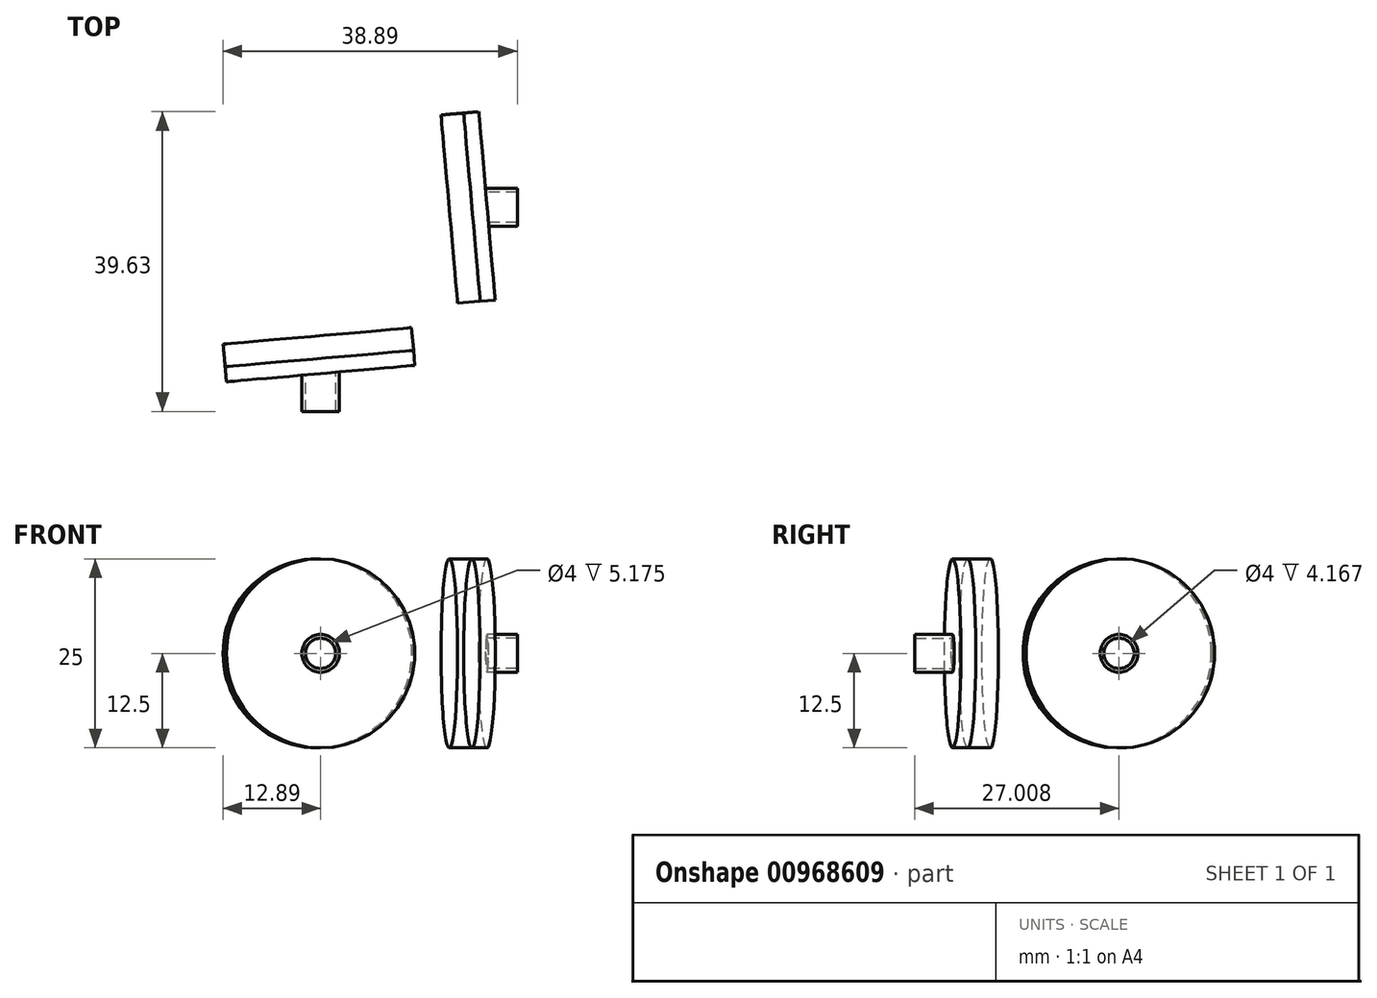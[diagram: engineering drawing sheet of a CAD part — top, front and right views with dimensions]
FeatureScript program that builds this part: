
annotation { "Feature Type Name" : "Feature", "Feature Type Description" : "" }
export const myFeature = defineFeature(function(context is Context, id is Id, definition is map)
    precondition{}
    {
        {
            var Q0;
            Q0=qCreatedBy(makeId("Top.planeOp"),FACE);
            var sketch = newSketch(context, id + "F0", { "sketchPlane" : qUnion([Q0])});
            skLineSegment(sketch, "E0", {"start": v(-12.45, -1.09) * mm, "end": v(0, 0) * mm});
            skLineSegment(sketch, "E1.0", {"start": v(-12.63, 0.9) * mm, "end": v(-0.17, 2) * mm});
            skLineSegment(sketch, "E2", {"start": v(-12.63, 0.9) * mm, "end": v(-12.45, -1.09) * mm});
            skLineSegment(sketch, "E3", {"start": v(-0.17, 2) * mm, "end": v(0, 0) * mm});
            skLineSegment(sketch, "E4", {"start": v(-3.25, 2.3) * mm, "end": v(0.17, 2) * mm, "construction": true});
            skLineSegment(sketch, "E5", {"start": v(-20, 22) * mm, "end": v(0, 2) * mm, "construction": true});
            skLineSegment(sketch, "E6", {"start": v(0.92, 12.5) * mm, "end": v(0, 2) * mm, "construction": true});
            skLineSegment(sketch, "E7", {"start": v(-0.82, 11.4) * mm, "end": v(0, 2) * mm, "construction": true});
            skLineSegment(sketch, "E8.MirrorCS", {"start": v(16.22, 25.18) * mm, "end": v(0, 2) * mm, "construction": true});
            skLineSegment(sketch, "E9.MirrorCS", {"start": v(23.17, 18.23) * mm, "end": v(0, 2) * mm, "construction": true});
            skLineSegment(sketch, "E10.MirrorCS", {"start": v(20, 22) * mm, "end": v(0, 2) * mm, "construction": true});
            skLineSegment(sketch, "E11", {"start": v(-20, 9.08) * mm, "end": v(-20, -14.55) * mm, "construction": true});
            skLineSegment(sketch, "E12", {"start": v(20, 39) * mm, "end": v(20, -14.55) * mm, "construction": true});
            skLineSegment(sketch, "E13", {"start": v(-20, -14.55) * mm, "end": v(0, -14.55) * mm, "construction": true});
            skLineSegment(sketch, "E14", {"start": v(20, -14.55) * mm, "end": v(0, -14.55) * mm, "construction": true});
            skLineSegment(sketch, "E15", {"start": v(18.91, 34.46) * mm, "end": v(20, 22) * mm});
            skLineSegment(sketch, "E16.0", {"start": v(20.9, 34.63) * mm, "end": v(22, 22.18) * mm});
            skLineSegment(sketch, "E17", {"start": v(22, 22.18) * mm, "end": v(20, 22) * mm});
            skLineSegment(sketch, "E18", {"start": v(20.9, 34.63) * mm, "end": v(18.91, 34.46) * mm});
            skSolve(sketch);
        }
        {
            var Q0;
            Q0=makeQuery(id+"F0.imprint","IMPRINT",FACE,{"disambiguationData":[TD([[makeQuery(id+"F0.imprint","IMPRINT",EDGE,{"derivedFrom":sQuery(id+"F0.wireOp",EDGE,"E0")}),1.0]])]});
            var Q1;
            Q1=sQuery(id+"F0.wireOp",EDGE,"E3");
            revolve(context, id + "F1", {"surfaceOperationType" : NewSurfaceOperationType.NEW, "entities" : qUnion([Q0]), "axis" : qUnion([Q1]), "revolveType" : RevolveType.FULL});
        }
        {
            var Q0;
            Q0=qCreatedBy(makeId("Front.planeOp"),FACE);
            var sketch = newSketch(context, id + "F2", { "sketchPlane" : qUnion([Q0])});
            skCircle(sketch, "E19", {"center": v(0, 0) * mm, "radius": 2.5 * mm});
            skCircle(sketch, "E20", {"center": v(0, 0) * mm, "radius": 2 * mm});
            skSolve(sketch);
        }
        {
            var Q0;
            Q0=makeQuery(id+"F2.imprint","IMPRINT",FACE,{"disambiguationData":[TD([[makeQuery(id+"F2.imprint","IMPRINT",EDGE,{"derivedFrom":sQuery(id+"F2.wireOp",EDGE,"E19")}),1.0]])]});
            extrude(context, id + "F3", {"entities" : qUnion([Q0]), "operationType" : NewBodyOperationType.ADD, "depth" : 5 * mm, "offsetDistance" : 25 * mm, "hasSecondDirection" : true, "secondDirectionOppositeDirection" : true, "secondDirectionDepth" : 1 * mm});
        }
        {
            var Q0;
            Q0=makeQuery(id+"F0.imprint","IMPRINT",FACE,{"disambiguationData":[TD([[makeQuery(id+"F0.imprint","IMPRINT",EDGE,{"derivedFrom":sQuery(id+"F0.wireOp",EDGE,"E15")}),1.0]])]});
            var Q1;
            Q1=sQuery(id+"F0.wireOp",EDGE,"E17");
            revolve(context, id + "F4", {"surfaceOperationType" : NewSurfaceOperationType.NEW, "entities" : qUnion([Q0]), "axis" : qUnion([Q1]), "revolveType" : RevolveType.FULL});
        }
        {
            var Q0;
            Q0=qCreatedBy(makeId("Right.planeOp"),FACE);
            var sketch = newSketch(context, id + "F5", { "sketchPlane" : qUnion([Q0])});
            skCircle(sketch, "E21", {"center": v(22, 0) * mm, "radius": 2.5 * mm});
            skCircle(sketch, "E22", {"center": v(22, 0) * mm, "radius": 2 * mm});
            skSolve(sketch);
        }
        {
            var Q0;
            Q0=makeQuery(id+"F5.imprint","IMPRINT",FACE,{"disambiguationData":[TD([[makeQuery(id+"F5.imprint","IMPRINT",EDGE,{"derivedFrom":sQuery(id+"F5.wireOp",EDGE,"E21")}),1.0]])]});
            extrude(context, id + "F6", {"entities" : qUnion([Q0]), "operationType" : NewBodyOperationType.ADD, "depth" : 26 * mm, "offsetDistance" : 25 * mm, "hasSecondDirection" : true, "secondDirectionOppositeDirection" : false, "secondDirectionDepth" : 21 * mm});
        }
        {
            var Q0;
            Q0=makeQuery(id+"F4.opRevolve","SWEPT_FACE",FACE,{"disambiguationData":[OSD([sQuery(id+"F0.wireOp",EDGE,"E15")])]});
            extrude(context, id + "F7", {"entities" : qUnion([Q0]), "depth" : 3 * mm, "offsetDistance" : 25 * mm});
        }
        {
            var Q0;
            Q0=makeQuery(id+"F1.opRevolve","SWEPT_FACE",FACE,{"disambiguationData":[OSD([sQuery(id+"F0.wireOp",EDGE,"E1.0")])]});
            extrude(context, id + "F8", {"entities" : qUnion([Q0]), "depth" : 3 * mm, "offsetDistance" : 25 * mm});
        }
    });
